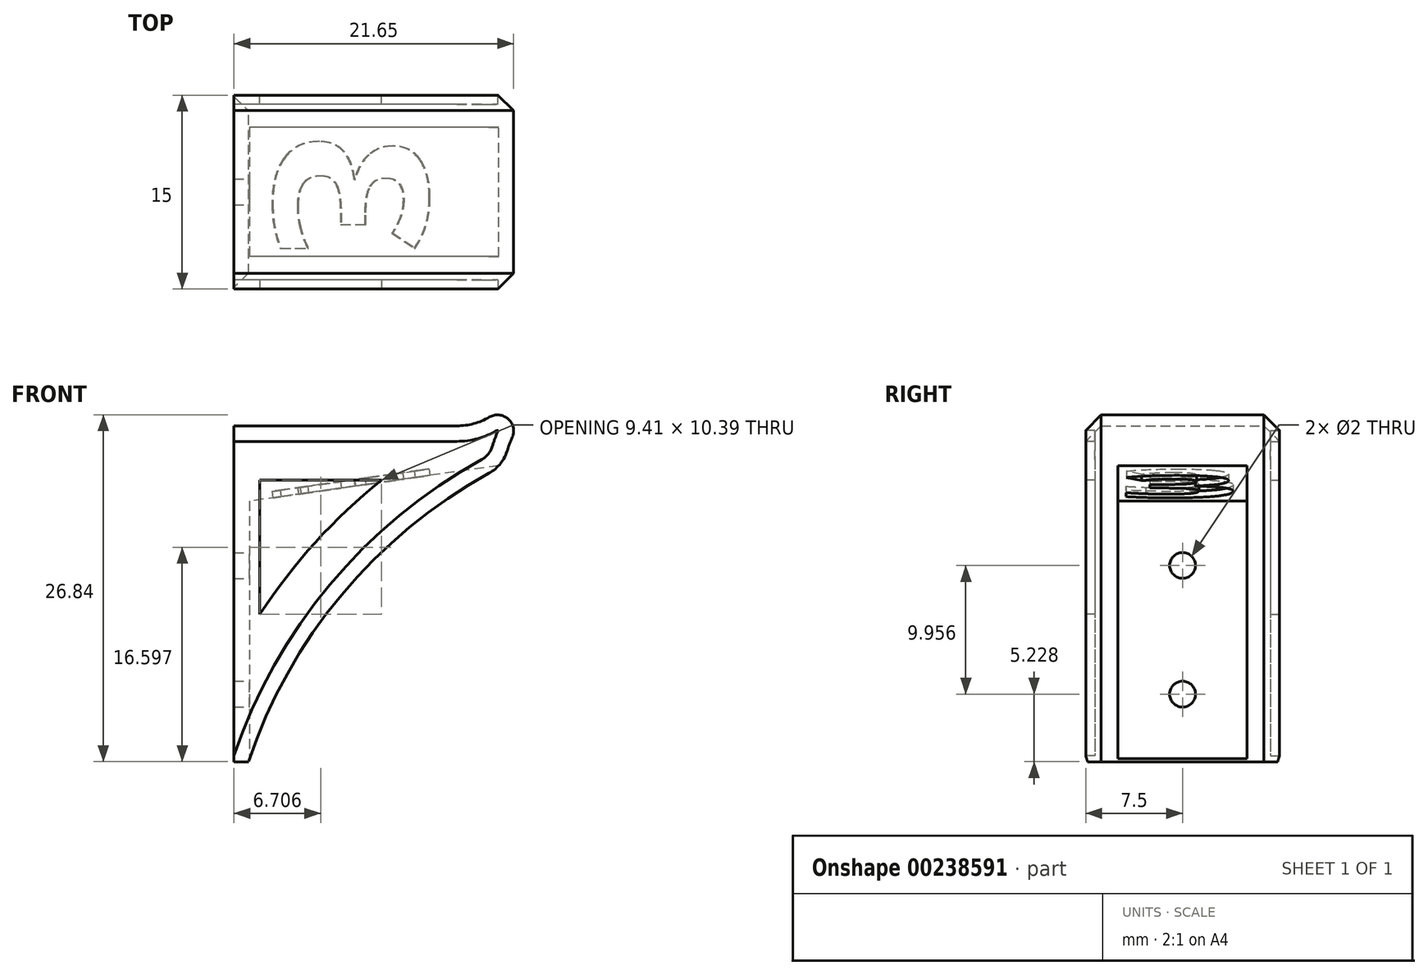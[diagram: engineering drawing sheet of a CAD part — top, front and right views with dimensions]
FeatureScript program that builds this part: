
annotation { "Feature Type Name" : "Feature", "Feature Type Description" : "" }
export const myFeature = defineFeature(function(context is Context, id is Id, definition is map)
    precondition{}
    {
        {
            var Q0;
            Q0=qCreatedBy(makeId("Front.planeOp"),FACE);
            var sketch = newSketch(context, id + "F0", { "sketchPlane" : qUnion([Q0])});
            skLineSegment(sketch, "E0", {"start": v(0, 30) * mm, "end": v(21, 30) * mm});
            skLineSegment(sketch, "E1", {"start": v(21, 30) * mm, "end": v(21, 27) * mm});
            skLineSegment(sketch, "E2", {"start": v(21, 27) * mm, "end": v(0, 24) * mm});
            skCircle(sketch, "E3", {"center": v(20.4, 29.6) * mm, "radius": 1.25 * mm});
            skLineSegment(sketch, "E4", {"start": v(0, 30) * mm, "end": v(0, 0) * mm});
            skArc(sketch, "E5", {"start": v(21, 27) * mm, "mid": v(7.47, 15.86) * mm, "end": v(0, 0) * mm});
            skLineSegment(sketch, "E6", {"start": v(1.2, 24.17) * mm, "end": v(1.2, 4.26) * mm});
            skSolve(sketch);
        }
        {
            var Q0;
            {var subQ0=sQuery(id+"F0.wireOp",EDGE,"E1");var subQ1=sQuery(id+"F0.wireOp",EDGE,"E0");var subQ2=makeQuery(id+"F0.imprint","INTERSECT",VERTEX,{"derivedFrom":[subQ1,subQ0]});Q0=makeQuery(id+"F0.imprint","IMPRINT",FACE,{"disambiguationData":[TD([[makeQuery(id+"F0.imprint","IMPRINT",EDGE,{"disambiguationData":[TD([[subQ2,1.0]])],"derivedFrom":subQ1}),1.0]])]});}
            var Q1;
            {var subQ0=sQuery(id+"F0.wireOp",EDGE,"E1");var subQ1=sQuery(id+"F0.wireOp",EDGE,"E0");var subQ2=makeQuery(id+"F0.imprint","INTERSECT",VERTEX,{"derivedFrom":[subQ1,subQ0]});Q1=makeQuery(id+"F0.imprint","IMPRINT",FACE,{"disambiguationData":[TD([[makeQuery(id+"F0.imprint","IMPRINT",EDGE,{"disambiguationData":[TD([[subQ2,1.0]])],"derivedFrom":subQ1}),-1.0]])]});}
            var Q2;
            {var subQ6=sQuery(id+"F0.wireOp",EDGE,"E4");var subQ8=sQuery(id+"F0.wireOp",EDGE,"E0");var subQ9=makeQuery(id+"F0.imprint","INTERSECT",VERTEX,{"derivedFrom":[subQ8,subQ6]});Q2=makeQuery(id+"F0.imprint","IMPRINT",FACE,{"disambiguationData":[TD([[makeQuery(id+"F0.imprint","IMPRINT",EDGE,{"disambiguationData":[TD([[subQ9,-1.0]])],"derivedFrom":subQ8}),-1.0]])]});}
            var Q3;
            {var subQ3=sQuery(id+"F0.wireOp",EDGE,"E6");Q3=makeQuery(id+"F0.imprint","IMPRINT",FACE,{"disambiguationData":[TD([[makeQuery(id+"F0.imprint","IMPRINT",EDGE,{"derivedFrom":subQ3}),1.0]])]});}
            var Q4;
            {var subQ3=sQuery(id+"F0.wireOp",EDGE,"E6");Q4=makeQuery(id+"F0.imprint","IMPRINT",FACE,{"disambiguationData":[TD([[makeQuery(id+"F0.imprint","IMPRINT",EDGE,{"derivedFrom":subQ3}),-1.0]])]});}
            extrude(context, id + "F1", {"entities" : qUnion([Q0, Q1, Q2, Q3, Q4]), "depth" : 15 * mm, "offsetDistance" : 25 * mm, "symmetric" : true});
        }
        {
            var Q0;
            Q0=makeQuery(id+"F1.opExtrude","SWEPT_EDGE",EDGE,{"disambiguationData":[OSD([sQuery(id+"F0.wireOp",EDGE,"E0"),sQuery(id+"F0.wireOp",EDGE,"E3")])]});
            var Q1;
            Q1=makeQuery(id+"F1.opExtrude","SWEPT_EDGE",EDGE,{"disambiguationData":[OSD([sQuery(id+"F0.wireOp",EDGE,"E1"),sQuery(id+"F0.wireOp",EDGE,"E3")])]});
            fillet(context, id + "F2", {"entities" : qUnion([Q0, Q1]), "radius" : 5 * mm, "tangentPropagation" : true, "allowEdgeOverflow" : false});
        }
        {
            var Q0;
            Q0=makeQuery(id+"F2.opFillet","BLEND_EDGE",EDGE,{"blendedFrom":[makeQuery(id+"F1.opExtrude","SWEPT_EDGE",EDGE,{"disambiguationData":[OSD([sQuery(id+"F0.wireOp",EDGE,"E1"),sQuery(id+"F0.wireOp",EDGE,"E3")])]}),makeQuery(id+"F1.opExtrude","SWEPT_FACE",FACE,{"disambiguationData":[OSD([sQuery(id+"F0.wireOp",EDGE,"E5")])]})],"blendedInto":[makeQuery(id+"F1.opExtrude","SWEPT_FACE",FACE,{"disambiguationData":[OSD([sQuery(id+"F0.wireOp",EDGE,"E5")])]})]});
            fillet(context, id + "F3", {"entities" : qUnion([Q0]), "radius" : 3 * mm, "tangentPropagation" : true, "allowEdgeOverflow" : false});
        }
        {
            var Q0;
            {var subQ3=sQuery(id+"F0.wireOp",EDGE,"E6");Q0=makeQuery(id+"F0.imprint","IMPRINT",FACE,{"disambiguationData":[TD([[makeQuery(id+"F0.imprint","IMPRINT",EDGE,{"derivedFrom":subQ3}),1.0]])]});}
            extrude(context, id + "F4", {"entities" : qUnion([Q0]), "operationType" : NewBodyOperationType.REMOVE, "oppositeDirection" : true, "depth" : 10 * mm, "offsetDistance" : 25 * mm, "symmetric" : true});
        }
        {
            var Q0;
            Q0=makeQuery(id+"F1.opExtrude","SWEPT_EDGE",EDGE,{"disambiguationData":[OSD([sQuery(id+"F0.wireOp",EDGE,"E4"),sQuery(id+"F0.wireOp",EDGE,"E5")])]});
            chamfer(context, id + "F5", {"entities" : qUnion([Q0]), "chamferType" : ChamferType.OFFSET_ANGLE, "width" : 5 * mm, "oppositeDirection" : true, "angle" : 90 * degree, "tangentPropagation" : true});
        }
        {
            var Q0;
            Q0=makeQuery(id+"F1.opExtrude","CAP_EDGE",EDGE,{"disambiguationData":[OSD([sQuery(id+"F0.wireOp",EDGE,"E0")])],"isStart":false});
            var Q1;
            Q1=makeQuery(id+"F1.opExtrude","CAP_EDGE",EDGE,{"disambiguationData":[OSD([sQuery(id+"F0.wireOp",EDGE,"E0")])],"isStart":true});
            chamfer(context, id + "F6", {"entities" : qUnion([Q0, Q1]), "width" : 1.2 * mm, "tangentPropagation" : true});
        }
        {
            var Q0;
            Q0=makeQuery(id+"F4.boolean.opBoolean","COPY",FACE,{"derivedFrom":makeQuery(id+"F4.opExtrude","SWEPT_FACE",FACE,{"disambiguationData":[OSD([sQuery(id+"F0.wireOp",EDGE,"E6")])]})});
            var sketch = newSketch(context, id + "F7", { "sketchPlane" : qUnion([Q0])});
            skCircle(sketch, "E7", {"center": v(0, 19.2) * mm, "radius": 1 * mm});
            skPoint(sketch, "E7.centerSnap0", {"position": v(0, 24.17) * mm});
            skCircle(sketch, "E8", {"center": v(0, 9.24) * mm, "radius": 1 * mm});
            skLineSegment(sketch, "E9", {"start": v(0, 19.2) * mm, "end": v(0, 24.17) * mm, "construction": true});
            skLineSegment(sketch, "E10", {"start": v(0, 9.24) * mm, "end": v(0, 4.26) * mm, "construction": true});
            skPoint(sketch, "E11", {"position": v(0, 14.22) * mm});
            skLineSegment(sketch, "E12", {"start": v(0, 19.2) * mm, "end": v(0, 14.22) * mm, "construction": true});
            skLineSegment(sketch, "E13", {"start": v(0, 14.22) * mm, "end": v(0, 9.24) * mm, "construction": true});
            skSolve(sketch);
        }
        {
            var Q0;
            Q0=makeQuery(id+"F7.imprint","IMPRINT",FACE,{"disambiguationData":[TD([[makeQuery(id+"F7.imprint","IMPRINT",EDGE,{"derivedFrom":sQuery(id+"F7.wireOp",EDGE,"E7")}),1.0]])]});
            var Q1;
            Q1=makeQuery(id+"F7.imprint","IMPRINT",FACE,{"disambiguationData":[TD([[makeQuery(id+"F7.imprint","IMPRINT",EDGE,{"derivedFrom":sQuery(id+"F7.wireOp",EDGE,"E8")}),1.0]])]});
            extrude(context, id + "F8", {"entities" : qUnion([Q0, Q1]), "operationType" : NewBodyOperationType.REMOVE, "endBound" : BoundingType.UP_TO_NEXT, "oppositeDirection" : true, "depth" : 25 * mm, "offsetDistance" : 25 * mm});
        }
        {
            var Q0;
            Q0=makeQuery(id+"F4.boolean.opBoolean","COPY",FACE,{"derivedFrom":makeQuery(id+"F4.opExtrude","SWEPT_FACE",FACE,{"disambiguationData":[OSD([sQuery(id+"F0.wireOp",EDGE,"E2")])]})});
            var sketch = newSketch(context, id + "F9", { "sketchPlane" : qUnion([Q0])});
            skText(sketch, "E14", { "text": "3", "fontName": "OpenSans-Bold.ttf"});
            const initialGuessF9  = {"E14": [0.0066, 0.005, 0, -1, 0.01206]};
            skSetInitialGuess(sketch, initialGuessF9);
            skSolve(sketch);
        }
        {
            var Q0;
            Q0 = qSketchRegion(id + "F9", true);
            extrude(context, id + "F10", {"entities" : qUnion([Q0]), "operationType" : NewBodyOperationType.REMOVE, "oppositeDirection" : true, "depth" : 0.5 * mm, "offsetDistance" : 25 * mm});
        }
        {
            var Q0;
            Q0=makeQuery(id+"F1.opExtrude","CAP_FACE",FACE,{"disambiguationData":[OSD([sQuery(id+"F0.wireOp",EDGE,"E0"),sQuery(id+"F0.wireOp",EDGE,"E1"),sQuery(id+"F0.wireOp",EDGE,"E3"),sQuery(id+"F0.wireOp",EDGE,"E4"),sQuery(id+"F0.wireOp",EDGE,"E5")])],"isStart":false});
            var sketch = newSketch(context, id + "F11", { "sketchPlane" : qUnion([Q0])});
            skArc(sketch, "E15.0", {"start": v(2, 15.41) * mm, "mid": v(6.3, 20.98) * mm, "end": v(11.41, 25.8) * mm});
            skLineSegment(sketch, "E15.2", {"start": v(11.41, 25.8) * mm, "end": v(2, 25.8) * mm});
            skLineSegment(sketch, "E16", {"start": v(2, 25.8) * mm, "end": v(2, 15.41) * mm});
            skSolve(sketch);
        }
        {
            var Q0;
            Q0=makeQuery(id+"F11.imprint","IMPRINT",FACE,{"disambiguationData":[TD([[makeQuery(id+"F11.imprint","IMPRINT",EDGE,{"derivedFrom":sQuery(id+"F11.wireOp",EDGE,"E15.0")}),1.0]])]});
            extrude(context, id + "F12", {"entities" : qUnion([Q0]), "oppositeDirection" : true, "depth" : 0.7 * mm, "offsetDistance" : 25 * mm});
        }
        {
            var Q0;
            Q0=makeQuery(id+"F12.opExtrude","SWEPT_BODY",BODY,{"disambiguationData":[OSD([sQuery(id+"F11.wireOp",EDGE,"E15.0"),sQuery(id+"F11.wireOp",EDGE,"E15.2"),sQuery(id+"F11.wireOp",EDGE,"E16")])]});
            var Q1;
            Q1=qCreatedBy(makeId("Front.planeOp"),FACE);
            mirror(context, id + "F13", {"entities" : qUnion([Q0]), "mirrorPlane" : qUnion([Q1])});
        }
        {
            var Q0;
            Q0=makeQuery(id+"F12.opExtrude","SWEPT_BODY",BODY,{"disambiguationData":[OSD([sQuery(id+"F11.wireOp",EDGE,"E15.0"),sQuery(id+"F11.wireOp",EDGE,"E15.2"),sQuery(id+"F11.wireOp",EDGE,"E16")])]});
            var Q1;
            Q1=makeQuery(id+"F13.opPattern","COPY",BODY,{"derivedFrom":makeQuery(id+"F12.opExtrude","SWEPT_BODY",BODY,{"disambiguationData":[OSD([sQuery(id+"F11.wireOp",EDGE,"E15.0"),sQuery(id+"F11.wireOp",EDGE,"E15.2"),sQuery(id+"F11.wireOp",EDGE,"E16")])]}),"instanceName":"1"});
            var Q2;
            Q2=makeQuery(id+"F1.opExtrude","SWEPT_BODY",BODY,{"disambiguationData":[OSD([sQuery(id+"F0.wireOp",EDGE,"E0"),sQuery(id+"F0.wireOp",EDGE,"E1"),sQuery(id+"F0.wireOp",EDGE,"E3"),sQuery(id+"F0.wireOp",EDGE,"E4"),sQuery(id+"F0.wireOp",EDGE,"E5")])]});
            booleanBodies(context, id + "F14", {"operationType" : BooleanOperationType.SUBTRACTION, "tools" : qUnion([Q0, Q1]), "targets" : qUnion([Q2])});
        }
    });
